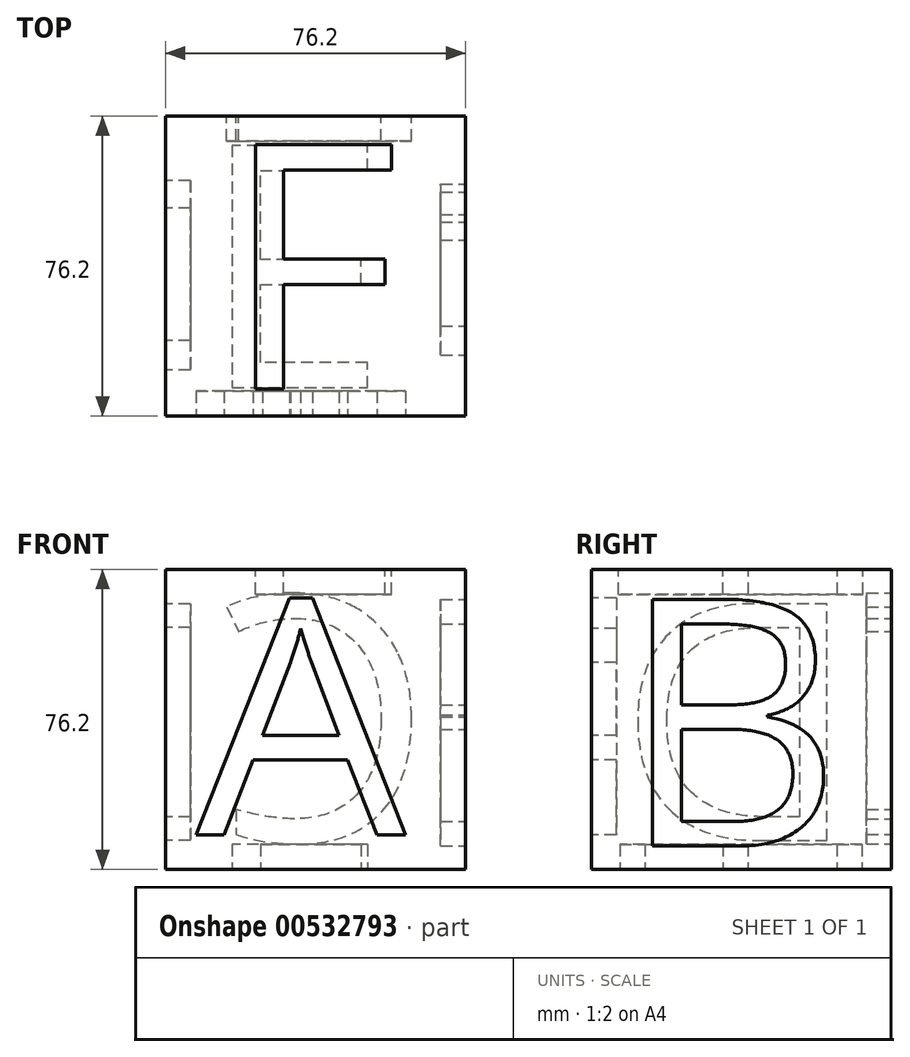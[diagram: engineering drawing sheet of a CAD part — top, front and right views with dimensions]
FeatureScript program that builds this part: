
annotation { "Feature Type Name" : "Feature", "Feature Type Description" : "" }
export const myFeature = defineFeature(function(context is Context, id is Id, definition is map)
    precondition{}
    {
        {
            var Q0;
            Q0=qCreatedBy(makeId("Front.planeOp"),FACE);
            var sketch = newSketch(context, id + "F0", { "sketchPlane" : qUnion([Q0])});
            skLineSegment(sketch, "E0.bottom", {"start": v(-50.34, -13.13) * mm, "end": v(25.86, -13.13) * mm});
            skLineSegment(sketch, "E0.top", {"start": v(-50.34, 63.07) * mm, "end": v(25.86, 63.07) * mm});
            skLineSegment(sketch, "E0.left", {"start": v(-50.34, -13.13) * mm, "end": v(-50.34, 63.07) * mm});
            skLineSegment(sketch, "E0.right", {"start": v(25.86, -13.13) * mm, "end": v(25.86, 63.07) * mm});
            skSolve(sketch);
        }
        {
            var Q0;
            Q0=makeQuery(id+"F0.imprint","IMPRINT",FACE,{"disambiguationData":[TD([[makeQuery(id+"F0.imprint","IMPRINT",EDGE,{"derivedFrom":sQuery(id+"F0.wireOp",EDGE,"E0.bottom")}),1.0]])]});
            extrude(context, id + "F1", {"entities" : qUnion([Q0]), "depth" : 76.2 * mm, "offsetDistance" : 25.4 * mm});
        }
        {
            var Q0;
            Q0=makeQuery(id+"F1.opExtrude","CAP_FACE",FACE,{"disambiguationData":[OSD([sQuery(id+"F0.wireOp",EDGE,"E0.bottom"),sQuery(id+"F0.wireOp",EDGE,"E0.top"),sQuery(id+"F0.wireOp",EDGE,"E0.left"),sQuery(id+"F0.wireOp",EDGE,"E0.right")])],"isStart":false});
            var sketch = newSketch(context, id + "F2", { "sketchPlane" : qUnion([Q0])});
            skText(sketch, "E1", { "text": "A", "fontName": "OpenSans-Regular.ttf"});
            const initialGuessF2  = {"E1": [-0.04256, -0.00442, 1, 0, 0.06047]};
            skSetInitialGuess(sketch, initialGuessF2);
            skSolve(sketch);
        }
        {
            var Q0;
            Q0 = qSketchRegion(id + "F2", true);
            extrude(context, id + "F3", {"entities" : qUnion([Q0]), "operationType" : NewBodyOperationType.REMOVE, "oppositeDirection" : true, "depth" : 6.35 * mm, "offsetDistance" : 25.4 * mm});
        }
        {
            var Q0;
            Q0=makeQuery(id+"F1.opExtrude","SWEPT_FACE",FACE,{"disambiguationData":[OSD([sQuery(id+"F0.wireOp",EDGE,"E0.right")])]});
            var sketch = newSketch(context, id + "F4", { "sketchPlane" : qUnion([Q0])});
            skText(sketch, "E2", { "text": "B", "fontName": "OpenSans-Regular.ttf"});
            const initialGuessF4  = {"E2": [-0.06931, -0.00721, 1, 0, 0.06326]};
            skSetInitialGuess(sketch, initialGuessF4);
            skSolve(sketch);
        }
        {
            var Q0;
            Q0 = qSketchRegion(id + "F4", true);
            extrude(context, id + "F5", {"entities" : qUnion([Q0]), "operationType" : NewBodyOperationType.REMOVE, "oppositeDirection" : true, "depth" : 6.35 * mm, "offsetDistance" : 25.4 * mm});
        }
        {
            var Q0;
            Q0=makeQuery(id+"F1.opExtrude","CAP_FACE",FACE,{"disambiguationData":[OSD([sQuery(id+"F0.wireOp",EDGE,"E0.bottom"),sQuery(id+"F0.wireOp",EDGE,"E0.top"),sQuery(id+"F0.wireOp",EDGE,"E0.left"),sQuery(id+"F0.wireOp",EDGE,"E0.right")])],"isStart":true});
            var sketch = newSketch(context, id + "F6", { "sketchPlane" : qUnion([Q0])});
            skText(sketch, "E3", { "text": "C", "fontName": "OpenSans-Regular.ttf"});
            const initialGuessF6  = {"E3": [-0.01744, -0.00581, 1, 0, 0.06257]};
            skSetInitialGuess(sketch, initialGuessF6);
            skSolve(sketch);
        }
        {
            var Q0;
            Q0 = qSketchRegion(id + "F6", true);
            extrude(context, id + "F7", {"entities" : qUnion([Q0]), "operationType" : NewBodyOperationType.REMOVE, "oppositeDirection" : true, "depth" : 6.35 * mm, "offsetDistance" : 25.4 * mm});
        }
        {
            var Q0;
            Q0=makeQuery(id+"F1.opExtrude","SWEPT_FACE",FACE,{"disambiguationData":[OSD([sQuery(id+"F0.wireOp",EDGE,"E0.left")])]});
            var sketch = newSketch(context, id + "F8", { "sketchPlane" : qUnion([Q0])});
            skText(sketch, "E4", { "text": "D", "fontName": "OpenSans-Regular.ttf"});
            const initialGuessF8  = {"E4": [0.00814, -0.00581, 1, 0, 0.0607]};
            skSetInitialGuess(sketch, initialGuessF8);
            skSolve(sketch);
        }
        {
            var Q0;
            Q0=makeQuery(id+"F8.imprint","IMPRINT",FACE,{"disambiguationData":[TD([[makeQuery(id+"F8.imprint","IMPRINT",EDGE,{"derivedFrom":sQuery(id+"F8.wireOp",EDGE,"E4.sketch_text.stroke-0")}),-1.0]])]});
            extrude(context, id + "F9", {"entities" : qUnion([Q0]), "operationType" : NewBodyOperationType.REMOVE, "oppositeDirection" : true, "depth" : 6.35 * mm, "offsetDistance" : 25.4 * mm});
        }
        {
            var Q0;
            Q0=makeQuery(id+"F1.opExtrude","SWEPT_FACE",FACE,{"disambiguationData":[OSD([sQuery(id+"F0.wireOp",EDGE,"E0.bottom")])]});
            var sketch = newSketch(context, id + "F10", { "sketchPlane" : qUnion([Q0])});
            skText(sketch, "E5", { "text": "E", "fontName": "OpenSans-Regular.ttf"});
            const initialGuessF10  = {"E5": [-0.04187, 0.00744, 1, 0, 0.0621]};
            skSetInitialGuess(sketch, initialGuessF10);
            skSolve(sketch);
        }
        {
            var Q0;
            Q0=makeQuery(id+"F10.imprint","IMPRINT",FACE,{"disambiguationData":[TD([[makeQuery(id+"F10.imprint","IMPRINT",EDGE,{"derivedFrom":sQuery(id+"F10.wireOp",EDGE,"E5.sketch_text.stroke-0")}),-1.0]])]});
            extrude(context, id + "F11", {"entities" : qUnion([Q0]), "operationType" : NewBodyOperationType.REMOVE, "oppositeDirection" : true, "depth" : 6.35 * mm, "offsetDistance" : 25.4 * mm});
        }
        {
            var Q0;
            Q0=makeQuery(id+"F1.opExtrude","SWEPT_FACE",FACE,{"disambiguationData":[OSD([sQuery(id+"F0.wireOp",EDGE,"E0.top")])]});
            var sketch = newSketch(context, id + "F12", { "sketchPlane" : qUnion([Q0])});
            skText(sketch, "E6", { "text": "F", "fontName": "OpenSans-Regular.ttf"});
            const initialGuessF12  = {"E6": [-0.03605, -0.06931, 1, 0, 0.06257]};
            skSetInitialGuess(sketch, initialGuessF12);
            skSolve(sketch);
        }
        {
            var Q0;
            Q0 = qSketchRegion(id + "F12", true);
            extrude(context, id + "F13", {"entities" : qUnion([Q0]), "operationType" : NewBodyOperationType.REMOVE, "oppositeDirection" : true, "depth" : 6.35 * mm, "offsetDistance" : 25.4 * mm});
        }
    });
